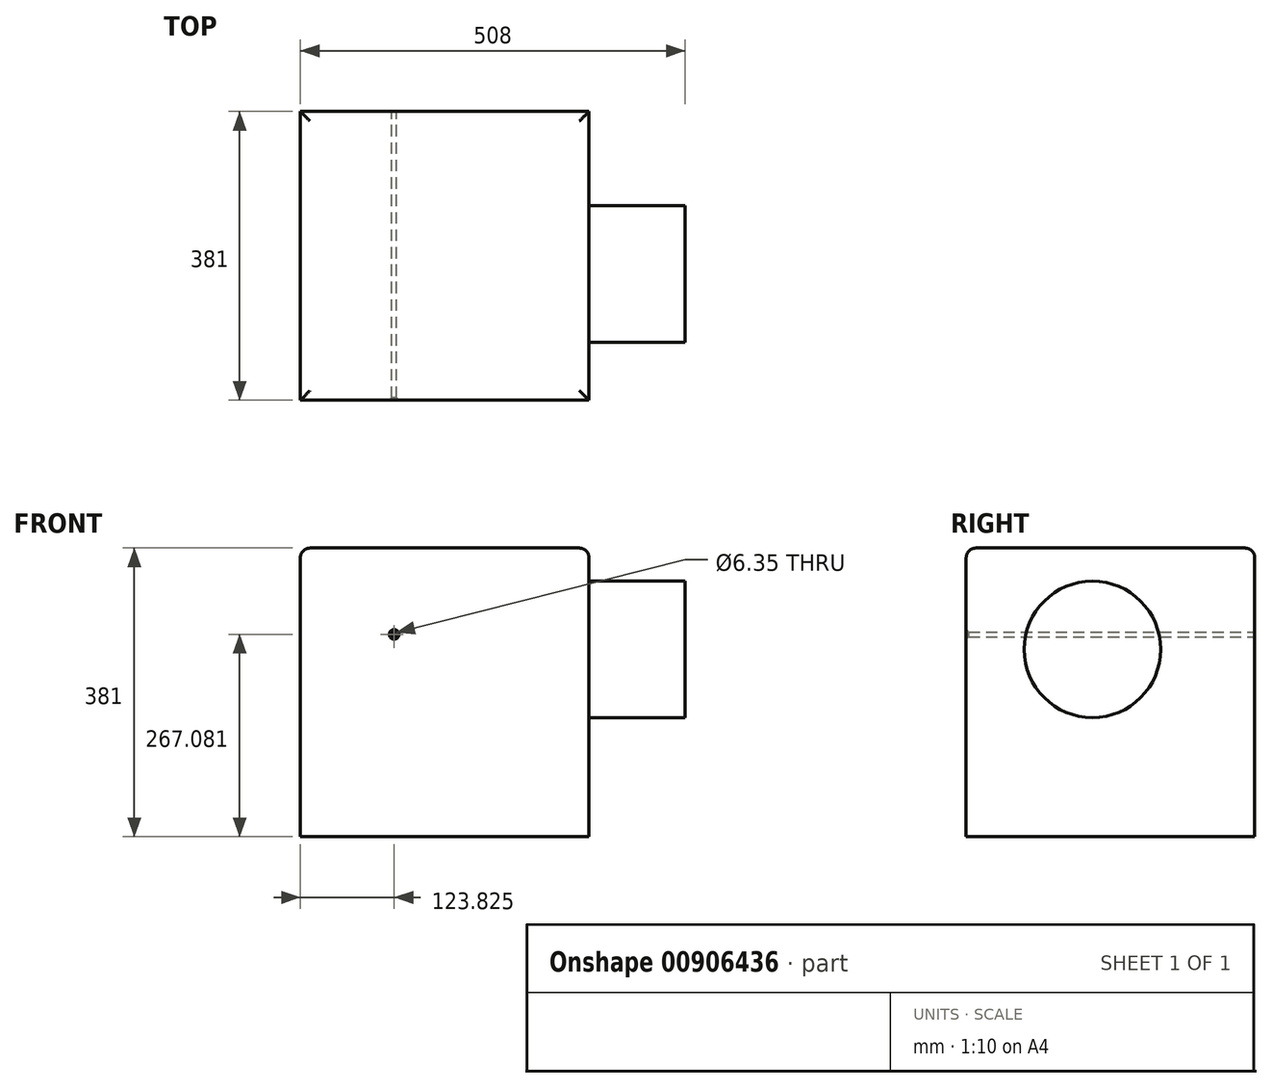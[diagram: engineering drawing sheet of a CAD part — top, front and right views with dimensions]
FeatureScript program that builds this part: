
annotation { "Feature Type Name" : "Feature", "Feature Type Description" : "" }
export const myFeature = defineFeature(function(context is Context, id is Id, definition is map)
    precondition{}
    {
        {
            var Q0;
            Q0=qCreatedBy(makeId("Front.planeOp"),FACE);
            var sketch = newSketch(context, id + "F0", { "sketchPlane" : qUnion([Q0])});
            skLineSegment(sketch, "E0.bottom", {"start": v(0, 0) * mm, "end": v(381, 0) * mm});
            skLineSegment(sketch, "E0.top", {"start": v(0, 381) * mm, "end": v(381, 381) * mm});
            skLineSegment(sketch, "E0.left", {"start": v(0, 0) * mm, "end": v(0, 381) * mm});
            skLineSegment(sketch, "E0.right", {"start": v(381, 0) * mm, "end": v(381, 381) * mm});
            skSolve(sketch);
        }
        {
            var Q0;
            Q0 = qSketchRegion(id + "F0", true);
            extrude(context, id + "F1", {"entities" : qUnion([Q0]), "depth" : 381 * mm, "offsetDistance" : 25.4 * mm});
        }
        {
            var Q0;
            Q0=makeQuery(id+"F1.opExtrude","CAP_FACE",FACE,{"disambiguationData":[OSD([sQuery(id+"F0.wireOp",EDGE,"E0.bottom"),sQuery(id+"F0.wireOp",EDGE,"E0.top"),sQuery(id+"F0.wireOp",EDGE,"E0.left"),sQuery(id+"F0.wireOp",EDGE,"E0.right")])],"isStart":false});
            var sketch = newSketch(context, id + "F2", { "sketchPlane" : qUnion([Q0])});
            skPoint(sketch, "E1", {"position": v(123.83, 267.08) * mm});
            skSolve(sketch);
        }
        {
            var Q0;
            Q0=sQuery(id+"F2.wireOp",VERTEX,"E1");
            var Q1;
            Q1=makeQuery(id+"F1.opExtrude","SWEPT_BODY",BODY,{"disambiguationData":[OSD([sQuery(id+"F0.wireOp",EDGE,"E0.bottom"),sQuery(id+"F0.wireOp",EDGE,"E0.top"),sQuery(id+"F0.wireOp",EDGE,"E0.left"),sQuery(id+"F0.wireOp",EDGE,"E0.right")])]});
            hole(context, id + "F3", {"style" : HoleStyle.C_SINK, "endStyle" : HoleEndStyle.THROUGH, "holeDiameter" : 6.35 * mm, "cSinkDiameter" : 12.7 * mm, "cSinkAngle" : 90 * degree, "majorDiameter" : 6.35 * mm, "isTappedThrough" : true, "tappedDepth" : 12.7 * mm, "tapClearance" : 3, "locations" : qUnion([Q0]), "scope" : qUnion([Q1]), "startStyle" : HoleStartStyle.PART});
        }
        {
            var Q0;
            Q0=makeQuery(id+"F1.opExtrude","SWEPT_FACE",FACE,{"disambiguationData":[OSD([sQuery(id+"F0.wireOp",EDGE,"E0.top")])]});
            fillet(context, id + "F4", {"entities" : qUnion([Q0]), "radius" : 12.7 * mm, "tangentPropagation" : true, "allowEdgeOverflow" : false});
        }
        {
            var Q0;
            Q0=makeQuery(id+"F1.opExtrude","SWEPT_FACE",FACE,{"disambiguationData":[OSD([sQuery(id+"F0.wireOp",EDGE,"E0.right")])]});
            var sketch = newSketch(context, id + "F5", { "sketchPlane" : qUnion([Q0])});
            skCircle(sketch, "E2", {"center": v(-214.3, 247.3) * mm, "radius": 90.07 * mm});
            skSolve(sketch);
        }
        {
            var Q0;
            Q0 = qSketchRegion(id + "F5", true);
            extrude(context, id + "F6", {"entities" : qUnion([Q0]), "operationType" : NewBodyOperationType.ADD, "depth" : 127 * mm, "offsetDistance" : 25.4 * mm});
        }
    });
